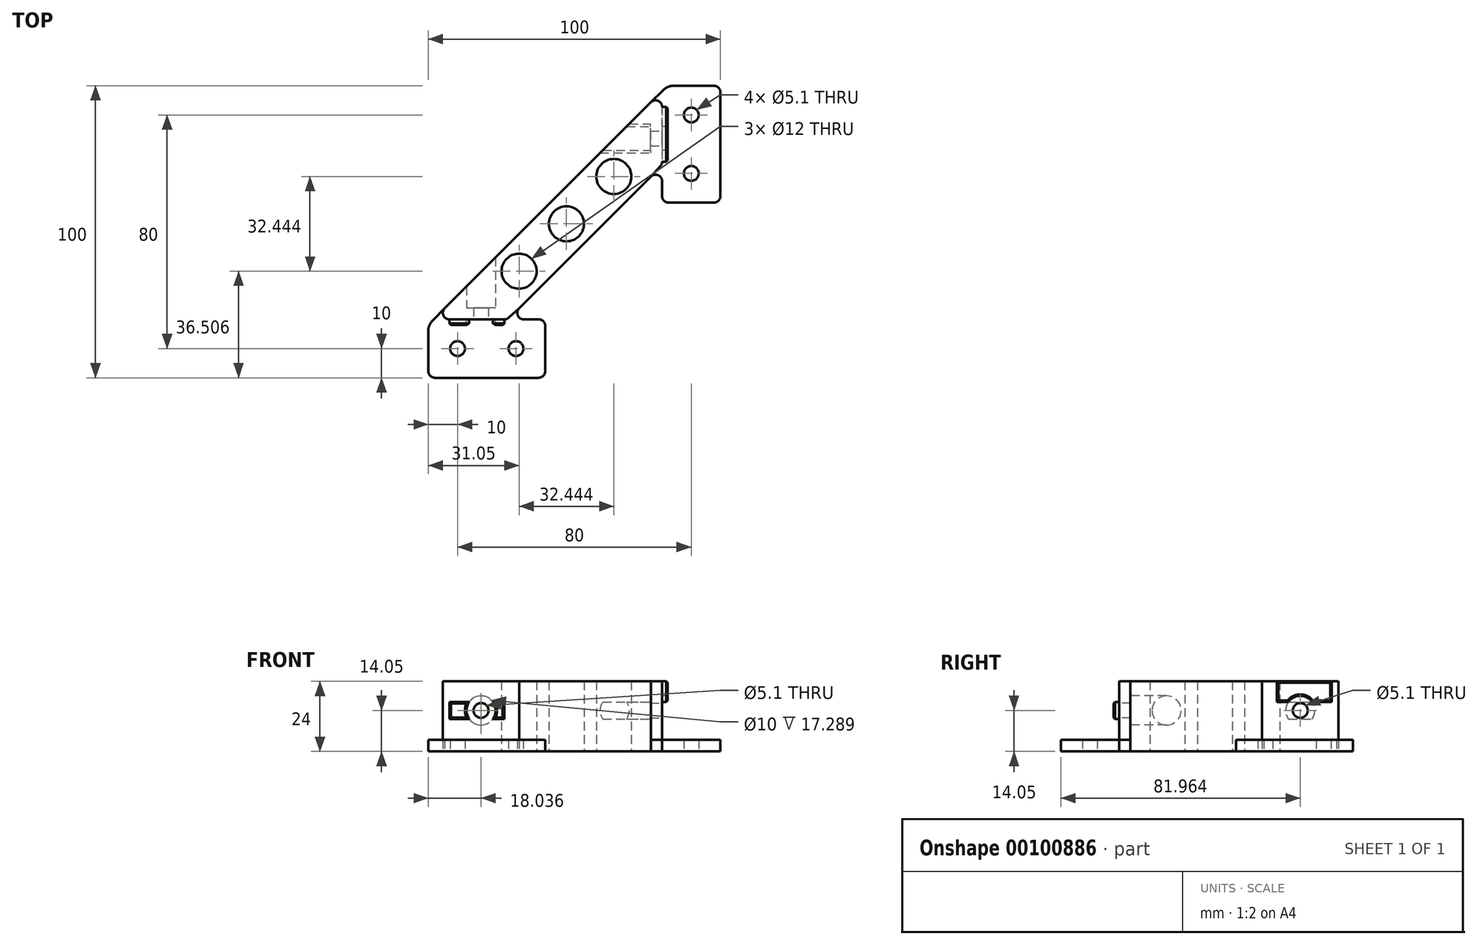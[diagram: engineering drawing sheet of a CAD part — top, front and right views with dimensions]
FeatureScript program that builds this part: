
annotation { "Feature Type Name" : "Feature", "Feature Type Description" : "" }
export const myFeature = defineFeature(function(context is Context, id is Id, definition is map)
    precondition{}
    {
        {
            var Q0;
            Q0=qCreatedBy(makeId("Top.planeOp"),FACE);
            var sketch = newSketch(context, id + "F0", { "sketchPlane" : qUnion([Q0])});
            skLineSegment(sketch, "E0.bottom", {"start": v(2.23, 0) * mm, "end": v(37.77, 0) * mm});
            skLineSegment(sketch, "E0.top", {"start": v(32.66, 20) * mm, "end": v(37.77, 20) * mm});
            skLineSegment(sketch, "E0.left", {"start": v(0, 2.23) * mm, "end": v(0, 16.11) * mm});
            skLineSegment(sketch, "E0.right", {"start": v(40, 2.23) * mm, "end": v(40, 17.77) * mm});
            skLineSegment(sketch, "E1", {"start": v(0, 0) * mm, "end": v(100, 0) * mm, "construction": true});
            skLineSegment(sketch, "E2", {"start": v(100, 0) * mm, "end": v(100, 100) * mm, "construction": true});
            skLineSegment(sketch, "E3.bottom", {"start": v(97.77, 100) * mm, "end": v(83.89, 100) * mm});
            skLineSegment(sketch, "E3.top", {"start": v(97.77, 60) * mm, "end": v(82.23, 60) * mm});
            skLineSegment(sketch, "E3.left", {"start": v(100, 97.77) * mm, "end": v(100, 62.23) * mm});
            skLineSegment(sketch, "E3.right", {"start": v(80, 67.34) * mm, "end": v(80, 62.23) * mm});
            skLineSegment(sketch, "E4", {"start": v(40, 20) * mm, "end": v(32, 20) * mm, "construction": true});
            skLineSegment(sketch, "E5", {"start": v(80, 60) * mm, "end": v(80, 68) * mm, "construction": true});
            skLineSegment(sketch, "E6", {"start": v(76.2, 68.92) * mm, "end": v(31.08, 23.8) * mm});
            skLineSegment(sketch, "E7", {"start": v(76.2, 94.37) * mm, "end": v(5.63, 23.8) * mm});
            skLineSegment(sketch, "E8", {"start": v(90, 80) * mm, "end": v(90, 70) * mm, "construction": true});
            skLineSegment(sketch, "E9", {"start": v(90, 80) * mm, "end": v(90, 90) * mm, "construction": true});
            skCircle(sketch, "E10", {"center": v(90, 90) * mm, "radius": 2.55 * mm});
            skCircle(sketch, "E11", {"center": v(90, 70) * mm, "radius": 2.55 * mm});
            skLineSegment(sketch, "E12", {"start": v(20, 10) * mm, "end": v(10, 10) * mm, "construction": true});
            skPoint(sketch, "E12.endSnap0", {"position": v(0, 10) * mm});
            skLineSegment(sketch, "E13", {"start": v(20, 10) * mm, "end": v(30, 10) * mm, "construction": true});
            skCircle(sketch, "E14", {"center": v(30, 10) * mm, "radius": 2.55 * mm});
            skCircle(sketch, "E15", {"center": v(10, 10) * mm, "radius": 2.55 * mm});
            skPoint(sketch, "E16.newPointA", {"position": v(32, 24.73) * mm});
            skArc(sketch, "E16.filletArc", {"start": v(31.08, 23.8) * mm, "mid": v(30.6, 21.38) * mm, "end": v(32.66, 20) * mm});
            skArc(sketch, "E17.filletArc", {"start": v(80, 67.34) * mm, "mid": v(78.62, 69.4) * mm, "end": v(76.2, 68.92) * mm});
            skLineSegment(sketch, "E18", {"start": v(80, 92.8) * mm, "end": v(80, 73.96) * mm});
            skLineSegment(sketch, "E19", {"start": v(7.2, 20) * mm, "end": v(26.04, 20) * mm});
            skCircle(sketch, "E20", {"center": v(31.05, 36.5) * mm, "radius": 6 * mm});
            skCircle(sketch, "E21", {"center": v(63.5, 68.95) * mm, "radius": 6 * mm});
            skCircle(sketch, "E22", {"center": v(47.27, 52.73) * mm, "radius": 6 * mm});
            skPoint(sketch, "E23.visualSharp", {"position": v(0, 20) * mm});
            skPoint(sketch, "E24.visualSharp", {"position": v(0, 0) * mm});
            skArc(sketch, "E24.filletArc", {"start": v(0, 2.23) * mm, "mid": v(0.65, 0.65) * mm, "end": v(2.23, 0) * mm});
            skPoint(sketch, "E25.visualSharp", {"position": v(40, 0) * mm});
            skArc(sketch, "E25.filletArc", {"start": v(37.77, 0) * mm, "mid": v(39.35, 0.65) * mm, "end": v(40, 2.23) * mm});
            skPoint(sketch, "E26.visualSharp", {"position": v(40, 20) * mm});
            skArc(sketch, "E26.filletArc", {"start": v(40, 17.77) * mm, "mid": v(39.35, 19.35) * mm, "end": v(37.77, 20) * mm});
            skPoint(sketch, "E27.visualSharp", {"position": v(100, 60) * mm});
            skArc(sketch, "E27.filletArc", {"start": v(97.77, 60) * mm, "mid": v(99.35, 60.65) * mm, "end": v(100, 62.23) * mm});
            skPoint(sketch, "E28.visualSharp", {"position": v(80, 60) * mm});
            skArc(sketch, "E28.filletArc", {"start": v(80, 62.23) * mm, "mid": v(80.65, 60.65) * mm, "end": v(82.23, 60) * mm});
            skPoint(sketch, "E29.visualSharp", {"position": v(100, 100) * mm});
            skArc(sketch, "E29.filletArc", {"start": v(100, 97.77) * mm, "mid": v(99.35, 99.35) * mm, "end": v(97.77, 100) * mm});
            skArc(sketch, "E30.filletArc", {"start": v(80, 92.8) * mm, "mid": v(78.62, 94.86) * mm, "end": v(76.2, 94.37) * mm});
            skLineSegment(sketch, "E31", {"start": v(79.35, 97.53) * mm, "end": v(76.2, 94.37) * mm});
            skLineSegment(sketch, "E32", {"start": v(76.2, 68.92) * mm, "end": v(79.42, 72.46) * mm});
            skArc(sketch, "E33.filletArc", {"start": v(79.42, 72.46) * mm, "mid": v(79.85, 73.16) * mm, "end": v(80, 73.96) * mm});
            skLineSegment(sketch, "E34", {"start": v(31.08, 23.8) * mm, "end": v(27.54, 20.58) * mm});
            skArc(sketch, "E35.filletArc", {"start": v(26.04, 20) * mm, "mid": v(26.84, 20.15) * mm, "end": v(27.54, 20.58) * mm});
            skArc(sketch, "E36.filletArc", {"start": v(5.63, 23.8) * mm, "mid": v(5.14, 21.38) * mm, "end": v(7.2, 20) * mm});
            skLineSegment(sketch, "E37", {"start": v(2.47, 20.65) * mm, "end": v(5.63, 23.8) * mm});
            skLineSegment(sketch, "E38", {"start": v(80, 60) * mm, "end": v(40, 20) * mm, "construction": true});
            skLineSegment(sketch, "E39", {"start": v(3.72, 21.9) * mm, "end": v(1.46, 19.65) * mm});
            skLineSegment(sketch, "E40", {"start": v(0, 17.77) * mm, "end": v(0, 18.18) * mm});
            skPoint(sketch, "E41.newPointA", {"position": v(0, 18.18) * mm});
            skArc(sketch, "E41.filletArc", {"start": v(1.46, 19.65) * mm, "mid": v(0.38, 18.03) * mm, "end": v(0, 16.11) * mm});
            skLineSegment(sketch, "E42", {"start": v(76.2, 94.37) * mm, "end": v(80.35, 98.54) * mm});
            skLineSegment(sketch, "E43", {"start": v(81.82, 100) * mm, "end": v(82.23, 100) * mm});
            skArc(sketch, "E44.filletArc", {"start": v(83.89, 100) * mm, "mid": v(81.97, 99.62) * mm, "end": v(80.35, 98.54) * mm});
            skLineSegment(sketch, "E45", {"start": v(63.5, 68.95) * mm, "end": v(57.13, 75.31) * mm, "construction": true});
            skLineSegment(sketch, "E46", {"start": v(47.27, 52.73) * mm, "end": v(40.9, 59.1) * mm, "construction": true});
            skLineSegment(sketch, "E47", {"start": v(31.05, 36.5) * mm, "end": v(24.69, 42.87) * mm, "construction": true});
            skSolve(sketch);
        }
        {
            var Q0;
            Q0=makeQuery(id+"F0.imprint","IMPRINT",FACE,{"disambiguationData":[TD([[makeQuery(id+"F0.imprint","IMPRINT",EDGE,{"derivedFrom":sQuery(id+"F0.wireOp",EDGE,"E0.bottom")}),1.0]])]});
            var Q1;
            Q1=makeQuery(id+"F0.imprint","IMPRINT",FACE,{"disambiguationData":[TD([[makeQuery(id+"F0.imprint","IMPRINT",EDGE,{"derivedFrom":sQuery(id+"F0.wireOp",EDGE,"E3.bottom")}),1.0]])]});
            extrude(context, id + "F1", {"entities" : qUnion([Q0, Q1]), "depth" : 4 * mm});
        }
        {
            var Q0;
            Q0=makeQuery(id+"F0.imprint","IMPRINT",FACE,{"disambiguationData":[TD([[makeQuery(id+"F0.imprint","IMPRINT",EDGE,{"derivedFrom":sQuery(id+"F0.wireOp",EDGE,"E6")}),-1.0]])]});
            extrude(context, id + "F2", {"entities" : qUnion([Q0]), "depth" : 24 * mm});
        }
        {
            var Q0;
            Q0=makeQuery(id+"F2.opExtrude","SWEPT_FACE",FACE,{"disambiguationData":[OSD([sQuery(id+"F0.wireOp",EDGE,"E18")])]});
            var sketch = newSketch(context, id + "F3", { "sketchPlane" : qUnion([Q0])});
            skCircle(sketch, "E48", {"center": v(81.96, 14.05) * mm, "radius": 2.55 * mm});
            skCircle(sketch, "E49", {"center": v(81.96, 14.05) * mm, "radius": 5 * mm});
            skLineSegment(sketch, "E50", {"start": v(73.96, 11.15) * mm, "end": v(92.8, 11.15) * mm});
            skLineSegment(sketch, "E51", {"start": v(76.92, 16.95) * mm, "end": v(73.96, 16.95) * mm});
            skLineSegment(sketch, "E52", {"start": v(73.96, 16.95) * mm, "end": v(92.8, 16.95) * mm});
            skLineSegment(sketch, "E53", {"start": v(81.96, 14.05) * mm, "end": v(73.96, 14.05) * mm, "construction": true});
            skLineSegment(sketch, "E54", {"start": v(75.28, 14.05) * mm, "end": v(75.28, 16.95) * mm, "construction": true});
            skLineSegment(sketch, "E55", {"start": v(75.28, 14.05) * mm, "end": v(75.28, 11.15) * mm, "construction": true});
            skLineSegment(sketch, "E56.bottom", {"start": v(84.86, 11.15) * mm, "end": v(79.06, 11.15) * mm});
            skLineSegment(sketch, "E56.top", {"start": v(84.86, 16.95) * mm, "end": v(79.06, 16.95) * mm});
            skLineSegment(sketch, "E56.left", {"start": v(84.86, 11.15) * mm, "end": v(84.86, 16.95) * mm});
            skLineSegment(sketch, "E56.right", {"start": v(79.06, 11.15) * mm, "end": v(79.06, 16.95) * mm});
            skSolve(sketch);
        }
        {
            var Q0;
            Q0=makeQuery(id+"F3.imprint","IMPRINT",FACE,{"disambiguationData":[TD([[makeQuery(id+"F3.imprint","IMPRINT",EDGE,{"derivedFrom":sQuery(id+"F3.wireOp",EDGE,"E48")}),1.0]])]});
            extrude(context, id + "F4", {"entities" : qUnion([Q0]), "operationType" : NewBodyOperationType.REMOVE, "oppositeDirection" : true, "depth" : 25 * mm});
        }
        {
            var Q0;
            Q0=makeQuery(id+"F3.imprint","IMPRINT",FACE,{"disambiguationData":[TD([[makeQuery(id+"F3.imprint","IMPRINT",EDGE,{"derivedFrom":sQuery(id+"F3.wireOp",EDGE,"E48")}),-1.0]])]});
            var Q1;
            {var subQ0=sQuery(id+"F3.wireOp",EDGE,"E52");var subQ1=sQuery(id+"F3.wireOp",EDGE,"E49");var subQ2=makeQuery(id+"F3.imprint","INTERSECT",VERTEX,{"disambiguationData":[OD(0.0)],"derivedFrom":[subQ1,subQ0]});Q1=makeQuery(id+"F3.imprint","IMPRINT",FACE,{"disambiguationData":[TD([[makeQuery(id+"F3.imprint","IMPRINT",EDGE,{"disambiguationData":[TD([[subQ2,1.0]])],"derivedFrom":subQ1}),1.0]])]});}
            var Q2;
            {var subQ0=sQuery(id+"F3.wireOp",EDGE,"E50");var subQ1=sQuery(id+"F3.wireOp",EDGE,"E49");var subQ2=makeQuery(id+"F3.imprint","INTERSECT",VERTEX,{"disambiguationData":[OD(0.0)],"derivedFrom":[subQ1,subQ0]});Q2=makeQuery(id+"F3.imprint","IMPRINT",FACE,{"disambiguationData":[TD([[makeQuery(id+"F3.imprint","IMPRINT",EDGE,{"disambiguationData":[TD([[subQ2,-1.0]])],"derivedFrom":subQ1}),1.0]])]});}
            var Q3;
            {var subQ5=sQuery(id+"F3.wireOp",EDGE,"E56.right");Q3=makeQuery(id+"F3.imprint","IMPRINT",FACE,{"disambiguationData":[TD([[makeQuery(id+"F3.imprint","IMPRINT",EDGE,{"derivedFrom":subQ5}),1.0]])]});}
            var Q4;
            {var subQ5=sQuery(id+"F3.wireOp",EDGE,"E56.left");Q4=makeQuery(id+"F3.imprint","IMPRINT",FACE,{"disambiguationData":[TD([[makeQuery(id+"F3.imprint","IMPRINT",EDGE,{"derivedFrom":subQ5}),-1.0]])]});}
            extrude(context, id + "F5", {"entities" : qUnion([Q0, Q1, Q2, Q3, Q4]), "operationType" : NewBodyOperationType.REMOVE, "oppositeDirection" : true, "depth" : 25 * mm, "hasSecondDirection" : true, "secondDirectionOppositeDirection" : true, "secondDirectionDepth" : 4 * mm});
        }
        {
            var Q0;
            {var subQ0=sQuery(id+"F3.wireOp",EDGE,"E52");var subQ1=sQuery(id+"F3.wireOp",EDGE,"E49");var subQ2=makeQuery(id+"F3.imprint","INTERSECT",VERTEX,{"disambiguationData":[OD(0.0)],"derivedFrom":[subQ1,subQ0]});Q0=makeQuery(id+"F3.imprint","IMPRINT",FACE,{"disambiguationData":[TD([[makeQuery(id+"F3.imprint","IMPRINT",EDGE,{"disambiguationData":[TD([[subQ2,-1.0]])],"derivedFrom":subQ1}),-1.0]])]});}
            var Q1;
            {var subQ0=sQuery(id+"F3.wireOp",EDGE,"E52");var subQ1=sQuery(id+"F3.wireOp",EDGE,"E49");var subQ2=makeQuery(id+"F3.imprint","INTERSECT",VERTEX,{"disambiguationData":[OD(1.0)],"derivedFrom":[subQ1,subQ0]});Q1=makeQuery(id+"F3.imprint","IMPRINT",FACE,{"disambiguationData":[TD([[makeQuery(id+"F3.imprint","IMPRINT",EDGE,{"disambiguationData":[TD([[subQ2,1.0]])],"derivedFrom":subQ1}),-1.0]])]});}
            extrude(context, id + "F6", {"entities" : qUnion([Q0, Q1]), "operationType" : NewBodyOperationType.ADD, "depth" : 1.9 * mm});
        }
        {
            var Q0;
            Q0=makeQuery(id+"F2.opExtrude","SWEPT_FACE",FACE,{"disambiguationData":[OSD([sQuery(id+"F0.wireOp",EDGE,"E19")])]});
            var sketch = newSketch(context, id + "F7", { "sketchPlane" : qUnion([Q0])});
            skLineSegment(sketch, "E57", {"start": v(18.04, 14.05) * mm, "end": v(26.04, 14.05) * mm, "construction": true});
            skCircle(sketch, "E58", {"center": v(18.04, 14.05) * mm, "radius": 2.55 * mm});
            skCircle(sketch, "E59", {"center": v(18.04, 14.05) * mm, "radius": 5 * mm});
            skLineSegment(sketch, "E60", {"start": v(26.04, 16.95) * mm, "end": v(7.2, 16.95) * mm});
            skLineSegment(sketch, "E61", {"start": v(26.04, 11.15) * mm, "end": v(7.2, 11.15) * mm});
            skLineSegment(sketch, "E62", {"start": v(28.9, 14.05) * mm, "end": v(28.9, 16.95) * mm, "construction": true});
            skLineSegment(sketch, "E63", {"start": v(25.05, 14.05) * mm, "end": v(25.05, 11.15) * mm, "construction": true});
            skLineSegment(sketch, "E64.bottom", {"start": v(20.94, 11.15) * mm, "end": v(15.14, 11.15) * mm});
            skLineSegment(sketch, "E64.top", {"start": v(20.94, 16.95) * mm, "end": v(15.14, 16.95) * mm});
            skLineSegment(sketch, "E64.left", {"start": v(20.94, 11.15) * mm, "end": v(20.94, 16.95) * mm});
            skLineSegment(sketch, "E64.right", {"start": v(15.14, 11.15) * mm, "end": v(15.14, 16.95) * mm});
            skSolve(sketch);
        }
        {
            var Q0;
            Q0=makeQuery(id+"F7.imprint","IMPRINT",FACE,{"disambiguationData":[TD([[makeQuery(id+"F7.imprint","IMPRINT",EDGE,{"derivedFrom":sQuery(id+"F7.wireOp",EDGE,"E58")}),1.0]])]});
            extrude(context, id + "F8", {"entities" : qUnion([Q0]), "operationType" : NewBodyOperationType.REMOVE, "oppositeDirection" : true, "depth" : 22.92 * mm});
        }
        {
            var Q0;
            Q0=makeQuery(id+"F7.imprint","IMPRINT",FACE,{"disambiguationData":[TD([[makeQuery(id+"F7.imprint","IMPRINT",EDGE,{"derivedFrom":sQuery(id+"F7.wireOp",EDGE,"E58")}),-1.0]])]});
            var Q1;
            {var subQ0=sQuery(id+"F7.wireOp",EDGE,"E60");var subQ1=sQuery(id+"F7.wireOp",EDGE,"E59");var subQ2=makeQuery(id+"F7.imprint","INTERSECT",VERTEX,{"disambiguationData":[OD(0.0)],"derivedFrom":[subQ1,subQ0]});Q1=makeQuery(id+"F7.imprint","IMPRINT",FACE,{"disambiguationData":[TD([[makeQuery(id+"F7.imprint","IMPRINT",EDGE,{"disambiguationData":[TD([[subQ2,1.0]])],"derivedFrom":subQ1}),1.0]])]});}
            var Q2;
            {var subQ0=sQuery(id+"F7.wireOp",EDGE,"E61");var subQ1=sQuery(id+"F7.wireOp",EDGE,"E59");var subQ2=makeQuery(id+"F7.imprint","INTERSECT",VERTEX,{"disambiguationData":[OD(0.0)],"derivedFrom":[subQ1,subQ0]});Q2=makeQuery(id+"F7.imprint","IMPRINT",FACE,{"disambiguationData":[TD([[makeQuery(id+"F7.imprint","IMPRINT",EDGE,{"disambiguationData":[TD([[subQ2,-1.0]])],"derivedFrom":subQ1}),1.0]])]});}
            var Q3;
            {var subQ5=sQuery(id+"F7.wireOp",EDGE,"E64.right");Q3=makeQuery(id+"F7.imprint","IMPRINT",FACE,{"disambiguationData":[TD([[makeQuery(id+"F7.imprint","IMPRINT",EDGE,{"derivedFrom":subQ5}),1.0]])]});}
            var Q4;
            {var subQ5=sQuery(id+"F7.wireOp",EDGE,"E64.left");Q4=makeQuery(id+"F7.imprint","IMPRINT",FACE,{"disambiguationData":[TD([[makeQuery(id+"F7.imprint","IMPRINT",EDGE,{"derivedFrom":subQ5}),-1.0]])]});}
            extrude(context, id + "F9", {"entities" : qUnion([Q0, Q1, Q2, Q3, Q4]), "operationType" : NewBodyOperationType.REMOVE, "oppositeDirection" : true, "depth" : 25 * mm, "hasSecondDirection" : true, "secondDirectionOppositeDirection" : true, "secondDirectionDepth" : 4 * mm});
        }
        {
            var Q0;
            {var subQ0=sQuery(id+"F7.wireOp",EDGE,"E60");var subQ1=sQuery(id+"F7.wireOp",EDGE,"E59");var subQ2=makeQuery(id+"F7.imprint","INTERSECT",VERTEX,{"disambiguationData":[OD(0.0)],"derivedFrom":[subQ1,subQ0]});Q0=makeQuery(id+"F7.imprint","IMPRINT",FACE,{"disambiguationData":[TD([[makeQuery(id+"F7.imprint","IMPRINT",EDGE,{"disambiguationData":[TD([[subQ2,-1.0]])],"derivedFrom":subQ1}),-1.0]])]});}
            var Q1;
            {var subQ0=sQuery(id+"F7.wireOp",EDGE,"E60");var subQ1=sQuery(id+"F7.wireOp",EDGE,"E59");var subQ2=makeQuery(id+"F7.imprint","INTERSECT",VERTEX,{"disambiguationData":[OD(1.0)],"derivedFrom":[subQ1,subQ0]});Q1=makeQuery(id+"F7.imprint","IMPRINT",FACE,{"disambiguationData":[TD([[makeQuery(id+"F7.imprint","IMPRINT",EDGE,{"disambiguationData":[TD([[subQ2,1.0]])],"derivedFrom":subQ1}),-1.0]])]});}
            extrude(context, id + "F10", {"entities" : qUnion([Q0, Q1]), "operationType" : NewBodyOperationType.ADD, "depth" : 1.9 * mm});
        }
        {
            var Q0;
            Q0=makeQuery(id+"F10.opExtrude","CAP_FACE",FACE,{"disambiguationData":[OSD([sQuery(id+"F0.wireOp",EDGE,"E19"),sQuery(id+"F0.wireOp",EDGE,"E35.filletArc"),sQuery(id+"F0.wireOp",EDGE,"E36.filletArc"),sQuery(id+"F7.wireOp",EDGE,"E58"),sQuery(id+"F7.wireOp",EDGE,"E60"),sQuery(id+"F7.wireOp",EDGE,"E61")])],"isStart":false});
            var Q1;
            Q1=makeQuery(id+"F6.opExtrude","CAP_FACE",FACE,{"disambiguationData":[OSD([sQuery(id+"F0.wireOp",EDGE,"E18"),sQuery(id+"F0.wireOp",EDGE,"E30.filletArc"),sQuery(id+"F0.wireOp",EDGE,"E33.filletArc"),sQuery(id+"F3.wireOp",EDGE,"E48"),sQuery(id+"F3.wireOp",EDGE,"E50"),sQuery(id+"F3.wireOp",EDGE,"E52")])],"isStart":false});
            chamfer(context, id + "F11", {"entities" : qUnion([Q0, Q1]), "width" : .5 * mm, "tangentPropagation" : true});
        }
    });
